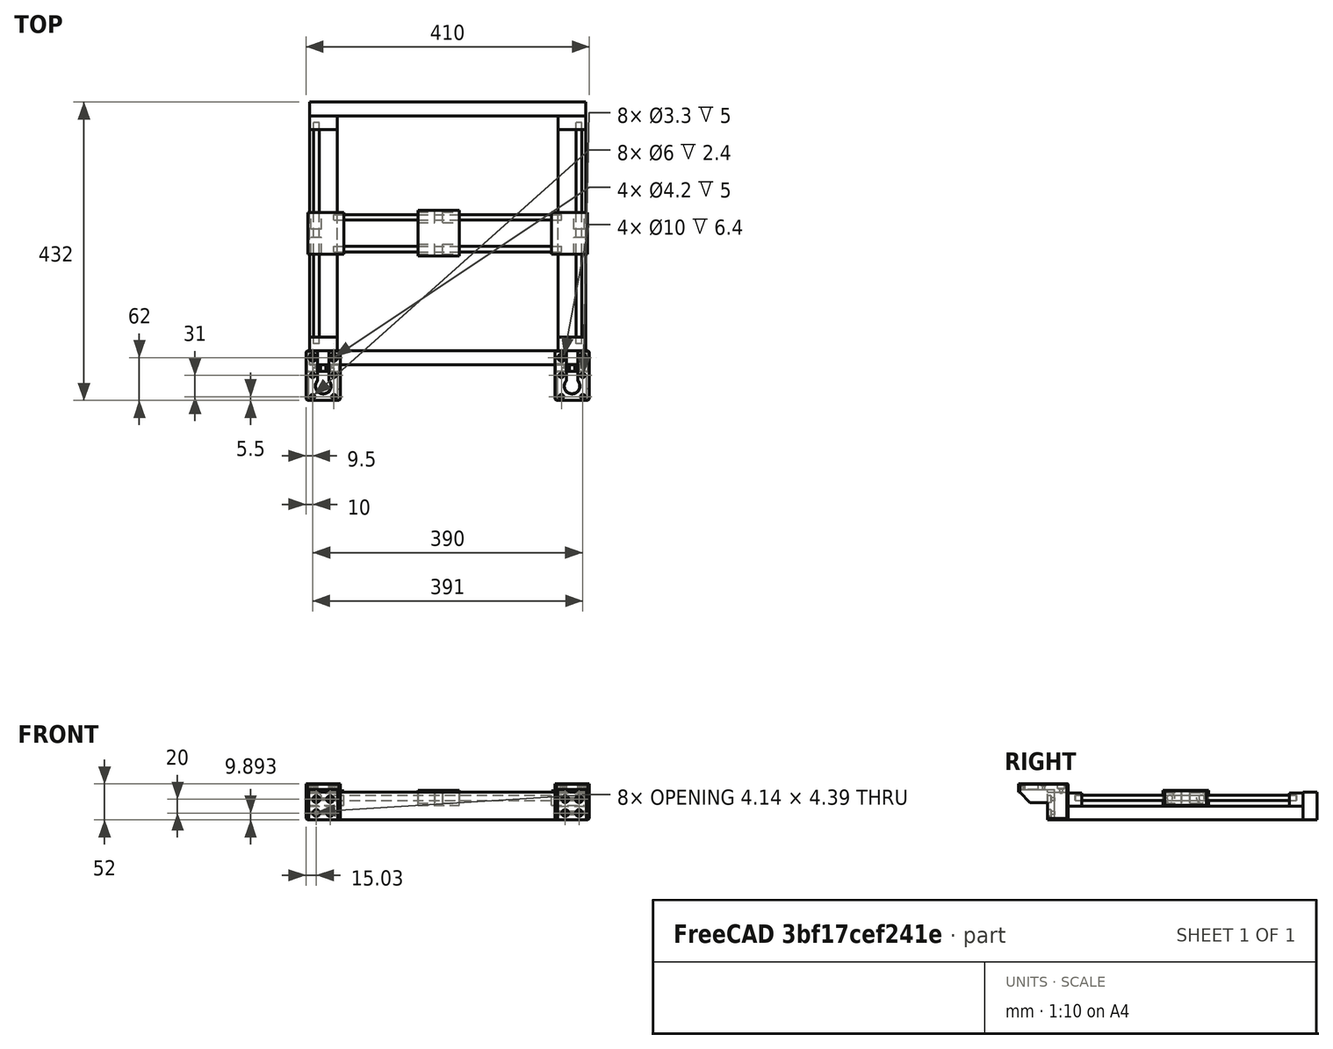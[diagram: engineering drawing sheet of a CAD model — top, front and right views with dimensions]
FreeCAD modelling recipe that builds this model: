
FCSTD DOCUMENT  (FreeCAD 0.18R14555 (Git shallow))
Label: overview
License: All rights reserved
LicenseURL: http://en.wikipedia.org/wiki/All_rights_reserved
objects: Part::Cylinder×12, Part::Box×11, App::DocumentObjectGroup×2, Part::Feature×2, Mesh::Feature×2
note: 25 computed .brp shape members not serialized (recipe doc carries the construction recipe); baked Part::Feature solids carry a one-line shape summary decoded from their .brp

FEATURE [Part::Box] Box  label="profile-04"
  AttacherType = Attacher::AttachEngine3D
  Height = 40
  Length = 400
  Placement = pos=(-185,0,0) rot=(0,0,1;0rad)
  Width = 20
FEATURE [Part::Box] Box001  label="profile-01"
  AttacherType = Attacher::AttachEngine3D
  Height = 20
  Length = 40
  Placement = pos=(-185,20,0) rot=(0,0,1;0rad)
  Width = 340
FEATURE [Part::Box] Box002  label="profile-02"
  AttacherType = Attacher::AttachEngine3D
  Height = 20
  Length = 40
  Placement = pos=(175,20,0) rot=(0,0,1;0rad)
  Width = 340
FEATURE [Part::Box] Box003  label="profile-03"
  AttacherType = Attacher::AttachEngine3D
  Height = 40
  Length = 400
  Placement = pos=(-185,360,0) rot=(0,0,1;0rad)
  Width = 20
FEATURE [Part::Cylinder] Cylinder  label="rod-01"
  Angle = 360
  AttacherType = Attacher::AttachEngine3D
  Height = 320
  Placement = pos=(-175,30,32) rot=(-1,0,0;1.5708rad)
  Radius = 4
FEATURE [Part::Cylinder] Cylinder001  label="rod-02"
  Angle = 360
  AttacherType = Attacher::AttachEngine3D
  Height = 320
  Placement = pos=(205,30,32) rot=(-1,0,0;1.5708rad)
  Radius = 4
FEATURE [Part::Cylinder] Cylinder002  label="rod-03"
  Angle = 360
  AttacherType = Attacher::AttachEngine3D
  Height = 330
  Placement = pos=(-150,167,32) rot=(0.57735,-0.57735,0.57735;4.18879rad)
  Radius = 4
FEATURE [Part::Cylinder] Cylinder003  label="rod-04"
  Angle = 360
  AttacherType = Attacher::AttachEngine3D
  Height = 330
  Placement = pos=(-150,213,32) rot=(0.57735,-0.57735,0.57735;4.18879rad)
  Radius = 4
FEATURE [Part::Cylinder] Cylinder004  label="bushing-01"
  Angle = 360
  AttacherType = Attacher::AttachEngine3D
  Height = 24
  Placement = pos=(-175,160,32) rot=(-1,0,0;1.5708rad)
  Radius = 7.5
FEATURE [Part::Cylinder] Cylinder005  label="bushing-02"
  Angle = 360
  AttacherType = Attacher::AttachEngine3D
  Height = 24
  Placement = pos=(205,160,32) rot=(-1,0,0;1.5708rad)
  Radius = 7.5
FEATURE [Part::Cylinder] Cylinder006  label="bushing-03"
  Angle = 360
  AttacherType = Attacher::AttachEngine3D
  Height = 24
  Placement = pos=(205,196,32) rot=(-1,0,0;1.5708rad)
  Radius = 7.5
FEATURE [Part::Cylinder] Cylinder007  label="bushing-04"
  Angle = 360
  AttacherType = Attacher::AttachEngine3D
  Height = 24
  Placement = pos=(-175,196,32) rot=(-1,0,0;1.5708rad)
  Radius = 7.5
FEATURE [Part::Cylinder] Cylinder008  label="bushing-05"
  Angle = 360
  AttacherType = Attacher::AttachEngine3D
  Height = 24
  Placement = pos=(-28,213,32) rot=(0.57735,-0.57735,0.57735;4.18879rad)
  Radius = 7.5
FEATURE [Part::Cylinder] Cylinder009  label="bushing-006"
  Angle = 360
  AttacherType = Attacher::AttachEngine3D
  Height = 24
  Placement = pos=(-28,167,32) rot=(0.57735,-0.57735,0.57735;4.18879rad)
  Radius = 7.5
FEATURE [Part::Cylinder] Cylinder010  label="bushing-007"
  Angle = 360
  AttacherType = Attacher::AttachEngine3D
  Height = 24
  Placement = pos=(8,213,32) rot=(0.57735,-0.57735,0.57735;4.18879rad)
  Radius = 7.5
FEATURE [Part::Cylinder] Cylinder011  label="bushing-008"
  Angle = 360
  AttacherType = Attacher::AttachEngine3D
  Height = 24
  Placement = pos=(8,167,32) rot=(0.57735,-0.57735,0.57735;4.18879rad)
  Radius = 7.5
FEATURE [Part::Box] Box004  label="Cube"
  AttacherType = Attacher::AttachEngine3D
  Height = 21
  Length = 52
  Placement = pos=(-187,160,21) rot=(0,0,1;0rad)
  Width = 60
FEATURE [Part::Box] Box005  label="Cube001"
  AttacherType = Attacher::AttachEngine3D
  Height = 21
  Length = 52
  Placement = pos=(165,160,21) rot=(0,0,1;0rad)
  Width = 60
FEATURE [Part::Box] Box006  label="Cube002"
  AttacherType = Attacher::AttachEngine3D
  Height = 22
  Length = 60
  Placement = pos=(-28,157,21) rot=(0,0,1;0rad)
  Width = 66
FEATURE [Part::Box] Box007  label="Cube003"
  AttacherType = Attacher::AttachEngine3D
  Height = 19
  Length = 40
  Placement = pos=(-185,340,20) rot=(0,0,1;0rad)
  Width = 20
FEATURE [Part::Box] Box008  label="Cube004"
  AttacherType = Attacher::AttachEngine3D
  Height = 19
  Length = 40
  Placement = pos=(175,340,20) rot=(0,0,1;0rad)
  Width = 20
FEATURE [Part::Box] Box009  label="Cube005"
  AttacherType = Attacher::AttachEngine3D
  Height = 19
  Length = 40
  Placement = pos=(175,20,20) rot=(0,0,1;0rad)
  Width = 20
FEATURE [Part::Box] Box010  label="Cube006"
  AttacherType = Attacher::AttachEngine3D
  Height = 19
  Length = 40
  Placement = pos=(-185,20,20) rot=(0,0,1;0rad)
  Width = 20
FEATURE [App::DocumentObjectGroup] Group  label="Frame"
  Group = -> [Box,Box001,Box002,Box003,Cylinder,Cylinder001,Cylinder002,Cylinder003,Cylinder004,Cylinder005,Cylinder006,Cylinder007,Cylinder008,Cylinder009,Cylinder010,Cylinder011,Box004,Box005,Box006,Box007,Box008,Box009,Box010]
FEATURE [Part::Feature] Chamfer005005001  label="motor-mount-left"
  Placement = pos=(-185,0,0) rot=(0,0,1;0rad)
  shape: bbox 50 x 72 x 52 mm, 204 faces (baked)
FEATURE [Part::Feature] Part__Mirroring001  label="motor-mount-right"
  Placement = pos=(215,0,0) rot=(0,0,1;0rad)
  shape: bbox 50 x 72 x 52 mm, 204 faces (baked)
FEATURE [Mesh::Feature] nema17v0  label="nema17-34-left"
  Placement = pos=(-186,-52,8) rot=(0,0,1;0rad)
FEATURE [Mesh::Feature] nema17v001  label="nema17-34-right"
  Placement = pos=(174,-52,8) rot=(0,0,1;0rad)
FEATURE [App::DocumentObjectGroup] Group001  label="Preference"
  Group = -> [nema17v0,nema17v001]
